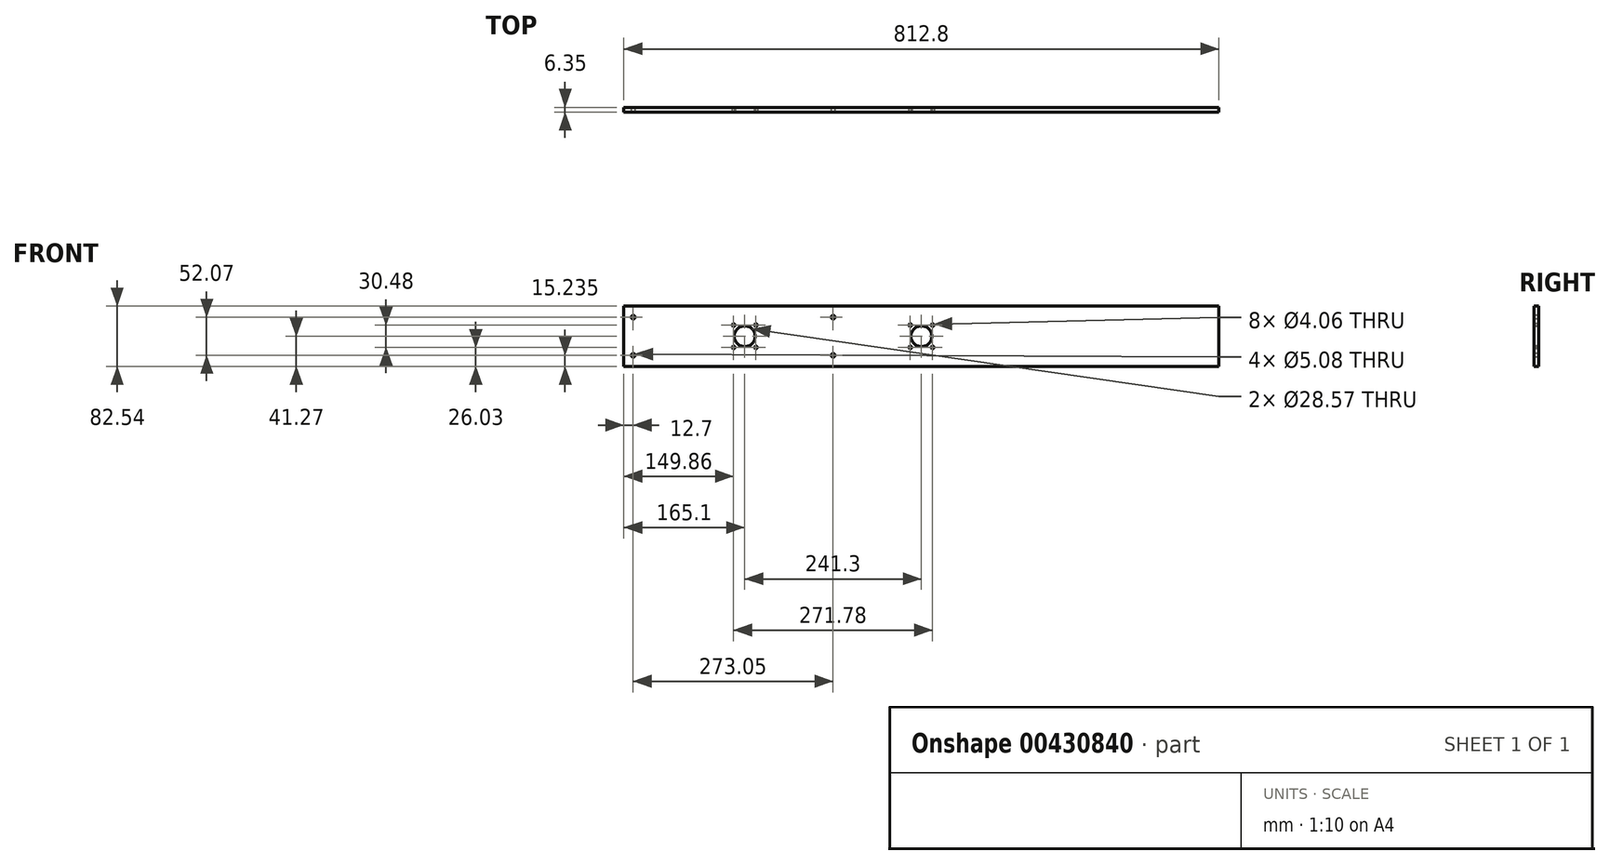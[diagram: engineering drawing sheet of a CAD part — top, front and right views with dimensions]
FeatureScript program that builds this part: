
annotation { "Feature Type Name" : "Feature", "Feature Type Description" : "" }
export const myFeature = defineFeature(function(context is Context, id is Id, definition is map)
    precondition{}
    {
        {
            var Q0;
            Q0=qCreatedBy(makeId("Front.planeOp"),FACE);
            var sketch = newSketch(context, id + "F0", { "sketchPlane" : qUnion([Q0])});
            skLineSegment(sketch, "E0.bottom", {"start": v(406.4, 41.28) * mm, "end": v(-406.4, 41.28) * mm});
            skLineSegment(sketch, "E0.top", {"start": v(406.4, -41.28) * mm, "end": v(-406.4, -41.28) * mm});
            skLineSegment(sketch, "E0.left", {"start": v(406.4, 41.28) * mm, "end": v(406.4, -41.28) * mm});
            skLineSegment(sketch, "E0.right", {"start": v(-406.4, 41.28) * mm, "end": v(-406.4, -41.28) * mm});
            skPoint(sketch, "E0.middle", {"position": v(0, 0) * mm});
            skSolve(sketch);
        }
        {
            var Q0;
            Q0=makeQuery(id+"F0.imprint","IMPRINT",FACE,{"disambiguationData":[TD([[makeQuery(id+"F0.imprint","IMPRINT",EDGE,{"derivedFrom":sQuery(id+"F0.wireOp",EDGE,"E0.bottom")}),1.0]])]});
            extrude(context, id + "F1", {"entities" : qUnion([Q0]), "depth" : 6.35 * mm});
        }
        {
            var Q0;
            Q0=makeQuery(id+"F1.opExtrude","CAP_FACE",FACE,{"disambiguationData":[OSD([sQuery(id+"F0.wireOp",EDGE,"E0.bottom"),sQuery(id+"F0.wireOp",EDGE,"E0.top"),sQuery(id+"F0.wireOp",EDGE,"E0.left"),sQuery(id+"F0.wireOp",EDGE,"E0.right")])],"isStart":false});
            var sketch = newSketch(context, id + "F2", { "sketchPlane" : qUnion([Q0])});
            skLineSegment(sketch, "E1", {"start": v(-406.4, 0) * mm, "end": v(-241.3, 0) * mm});
            skLineSegment(sketch, "E2", {"start": v(-241.3, 0) * mm, "end": v(-241.3, 15.24) * mm});
            skLineSegment(sketch, "E3", {"start": v(-241.3, 15.24) * mm, "end": v(-256.54, 15.24) * mm});
            skLineSegment(sketch, "E4", {"start": v(-256.54, 15.24) * mm, "end": v(-256.54, -15.24) * mm});
            skLineSegment(sketch, "E5", {"start": v(-256.54, -15.24) * mm, "end": v(-226.06, -15.24) * mm});
            skLineSegment(sketch, "E6", {"start": v(-226.06, -15.24) * mm, "end": v(-226.06, 15.24) * mm});
            skCircle(sketch, "E7", {"center": v(-256.54, 15.24) * mm, "radius": 2.03 * mm});
            skCircle(sketch, "E8", {"center": v(-256.54, -15.24) * mm, "radius": 2.03 * mm});
            skCircle(sketch, "E9", {"center": v(-226.06, -15.24) * mm, "radius": 2.03 * mm});
            skCircle(sketch, "E10", {"center": v(-226.06, 15.24) * mm, "radius": 2.03 * mm});
            skCircle(sketch, "E11", {"center": v(-241.3, 0) * mm, "radius": 14.29 * mm});
            skLineSegment(sketch, "E12", {"start": v(0, 0) * mm, "end": v(0, 15.24) * mm});
            skLineSegment(sketch, "E13", {"start": v(0, 15.24) * mm, "end": v(-15.24, 15.24) * mm});
            skLineSegment(sketch, "E14", {"start": v(-15.24, 15.24) * mm, "end": v(-15.24, -15.24) * mm});
            skLineSegment(sketch, "E15", {"start": v(-15.24, -15.24) * mm, "end": v(15.24, -15.24) * mm});
            skLineSegment(sketch, "E16", {"start": v(15.24, -15.24) * mm, "end": v(15.24, 15.24) * mm});
            skCircle(sketch, "E17", {"center": v(-15.24, 15.24) * mm, "radius": 2.03 * mm});
            skCircle(sketch, "E18", {"center": v(-15.24, -15.24) * mm, "radius": 2.03 * mm});
            skCircle(sketch, "E19", {"center": v(15.24, -15.24) * mm, "radius": 2.03 * mm});
            skCircle(sketch, "E20", {"center": v(15.24, 15.24) * mm, "radius": 2.03 * mm});
            skCircle(sketch, "E21", {"center": v(0, 0) * mm, "radius": 14.29 * mm});
            skSolve(sketch);
        }
        {
            var Q0;
            {var subQ0=sQuery(id+"F2.wireOp",EDGE,"E4");var subQ1=sQuery(id+"F2.wireOp",EDGE,"E3");var subQ2=makeQuery(id+"F2.imprint","INTERSECT",VERTEX,{"derivedFrom":[subQ1,subQ0]});Q0=makeQuery(id+"F2.imprint","IMPRINT",FACE,{"disambiguationData":[TD([[makeQuery(id+"F2.imprint","IMPRINT",EDGE,{"disambiguationData":[TD([[subQ2,1.0]])],"derivedFrom":subQ1}),-1.0]])]});}
            var Q1;
            {var subQ0=sQuery(id+"F2.wireOp",EDGE,"E4");var subQ1=sQuery(id+"F2.wireOp",EDGE,"E3");var subQ2=makeQuery(id+"F2.imprint","INTERSECT",VERTEX,{"derivedFrom":[subQ1,subQ0]});Q1=makeQuery(id+"F2.imprint","IMPRINT",FACE,{"disambiguationData":[TD([[makeQuery(id+"F2.imprint","IMPRINT",EDGE,{"disambiguationData":[TD([[subQ2,1.0]])],"derivedFrom":subQ1}),1.0]])]});}
            var Q2;
            {var subQ0=sQuery(id+"F2.wireOp",EDGE,"E2");var subQ1=sQuery(id+"F2.wireOp",EDGE,"E1");var subQ2=makeQuery(id+"F2.imprint","INTERSECT",VERTEX,{"derivedFrom":[subQ1,subQ0]});Q2=makeQuery(id+"F2.imprint","IMPRINT",FACE,{"disambiguationData":[TD([[makeQuery(id+"F2.imprint","IMPRINT",EDGE,{"disambiguationData":[TD([[subQ2,1.0]])],"derivedFrom":subQ1}),-1.0]])]});}
            var Q3;
            {var subQ0=sQuery(id+"F2.wireOp",EDGE,"E2");var subQ1=sQuery(id+"F2.wireOp",EDGE,"E1");var subQ2=makeQuery(id+"F2.imprint","INTERSECT",VERTEX,{"derivedFrom":[subQ1,subQ0]});Q3=makeQuery(id+"F2.imprint","IMPRINT",FACE,{"disambiguationData":[TD([[makeQuery(id+"F2.imprint","IMPRINT",EDGE,{"disambiguationData":[TD([[subQ2,1.0]])],"derivedFrom":subQ1}),1.0]])]});}
            var Q4;
            {var subQ0=sQuery(id+"F2.wireOp",EDGE,"E5");var subQ1=sQuery(id+"F2.wireOp",EDGE,"E4");var subQ2=makeQuery(id+"F2.imprint","INTERSECT",VERTEX,{"derivedFrom":[subQ1,subQ0]});Q4=makeQuery(id+"F2.imprint","IMPRINT",FACE,{"disambiguationData":[TD([[makeQuery(id+"F2.imprint","IMPRINT",EDGE,{"disambiguationData":[TD([[subQ2,1.0]])],"derivedFrom":subQ1}),-1.0]])]});}
            var Q5;
            {var subQ0=sQuery(id+"F2.wireOp",EDGE,"E5");var subQ1=sQuery(id+"F2.wireOp",EDGE,"E4");var subQ2=makeQuery(id+"F2.imprint","INTERSECT",VERTEX,{"derivedFrom":[subQ1,subQ0]});Q5=makeQuery(id+"F2.imprint","IMPRINT",FACE,{"disambiguationData":[TD([[makeQuery(id+"F2.imprint","IMPRINT",EDGE,{"disambiguationData":[TD([[subQ2,1.0]])],"derivedFrom":subQ1}),1.0]])]});}
            var Q6;
            {var subQ0=sQuery(id+"F2.wireOp",EDGE,"E6");var subQ1=sQuery(id+"F2.wireOp",EDGE,"E5");var subQ2=makeQuery(id+"F2.imprint","INTERSECT",VERTEX,{"derivedFrom":[subQ1,subQ0]});Q6=makeQuery(id+"F2.imprint","IMPRINT",FACE,{"disambiguationData":[TD([[makeQuery(id+"F2.imprint","IMPRINT",EDGE,{"disambiguationData":[TD([[subQ2,1.0]])],"derivedFrom":subQ1}),-1.0]])]});}
            var Q7;
            {var subQ0=sQuery(id+"F2.wireOp",EDGE,"E6");var subQ1=sQuery(id+"F2.wireOp",EDGE,"E5");var subQ2=makeQuery(id+"F2.imprint","INTERSECT",VERTEX,{"derivedFrom":[subQ1,subQ0]});Q7=makeQuery(id+"F2.imprint","IMPRINT",FACE,{"disambiguationData":[TD([[makeQuery(id+"F2.imprint","IMPRINT",EDGE,{"disambiguationData":[TD([[subQ2,1.0]])],"derivedFrom":subQ1}),1.0]])]});}
            var Q8;
            Q8=makeQuery(id+"F2.imprint","IMPRINT",FACE,{"disambiguationData":[TD([[makeQuery(id+"F2.imprint","IMPRINT",EDGE,{"derivedFrom":sQuery(id+"F2.wireOp",EDGE,"E10")}),1.0]])]});
            var Q9;
            Q9=makeQuery(id+"F2.imprint","IMPRINT",FACE,{"disambiguationData":[TD([[makeQuery(id+"F2.imprint","IMPRINT",EDGE,{"derivedFrom":sQuery(id+"F2.wireOp",EDGE,"E21")}),1.0]])]});
            var Q10;
            {var subQ0=sQuery(id+"F2.wireOp",EDGE,"E16");var subQ1=sQuery(id+"F2.wireOp",EDGE,"E15");var subQ2=makeQuery(id+"F2.imprint","INTERSECT",VERTEX,{"derivedFrom":[subQ1,subQ0]});Q10=makeQuery(id+"F2.imprint","IMPRINT",FACE,{"disambiguationData":[TD([[makeQuery(id+"F2.imprint","IMPRINT",EDGE,{"disambiguationData":[TD([[subQ2,1.0]])],"derivedFrom":subQ1}),-1.0]])]});}
            var Q11;
            {var subQ0=sQuery(id+"F2.wireOp",EDGE,"E16");var subQ1=sQuery(id+"F2.wireOp",EDGE,"E15");var subQ2=makeQuery(id+"F2.imprint","INTERSECT",VERTEX,{"derivedFrom":[subQ1,subQ0]});Q11=makeQuery(id+"F2.imprint","IMPRINT",FACE,{"disambiguationData":[TD([[makeQuery(id+"F2.imprint","IMPRINT",EDGE,{"disambiguationData":[TD([[subQ2,1.0]])],"derivedFrom":subQ1}),1.0]])]});}
            var Q12;
            Q12=makeQuery(id+"F2.imprint","IMPRINT",FACE,{"disambiguationData":[TD([[makeQuery(id+"F2.imprint","IMPRINT",EDGE,{"derivedFrom":sQuery(id+"F2.wireOp",EDGE,"E20")}),1.0]])]});
            var Q13;
            {var subQ0=sQuery(id+"F2.wireOp",EDGE,"E14");var subQ1=sQuery(id+"F2.wireOp",EDGE,"E13");var subQ2=makeQuery(id+"F2.imprint","INTERSECT",VERTEX,{"derivedFrom":[subQ1,subQ0]});Q13=makeQuery(id+"F2.imprint","IMPRINT",FACE,{"disambiguationData":[TD([[makeQuery(id+"F2.imprint","IMPRINT",EDGE,{"disambiguationData":[TD([[subQ2,1.0]])],"derivedFrom":subQ1}),-1.0]])]});}
            var Q14;
            {var subQ0=sQuery(id+"F2.wireOp",EDGE,"E14");var subQ1=sQuery(id+"F2.wireOp",EDGE,"E13");var subQ2=makeQuery(id+"F2.imprint","INTERSECT",VERTEX,{"derivedFrom":[subQ1,subQ0]});Q14=makeQuery(id+"F2.imprint","IMPRINT",FACE,{"disambiguationData":[TD([[makeQuery(id+"F2.imprint","IMPRINT",EDGE,{"disambiguationData":[TD([[subQ2,1.0]])],"derivedFrom":subQ1}),1.0]])]});}
            var Q15;
            {var subQ0=sQuery(id+"F2.wireOp",EDGE,"E15");var subQ1=sQuery(id+"F2.wireOp",EDGE,"E14");var subQ2=makeQuery(id+"F2.imprint","INTERSECT",VERTEX,{"derivedFrom":[subQ1,subQ0]});Q15=makeQuery(id+"F2.imprint","IMPRINT",FACE,{"disambiguationData":[TD([[makeQuery(id+"F2.imprint","IMPRINT",EDGE,{"disambiguationData":[TD([[subQ2,1.0]])],"derivedFrom":subQ1}),-1.0]])]});}
            var Q16;
            {var subQ0=sQuery(id+"F2.wireOp",EDGE,"E15");var subQ1=sQuery(id+"F2.wireOp",EDGE,"E14");var subQ2=makeQuery(id+"F2.imprint","INTERSECT",VERTEX,{"derivedFrom":[subQ1,subQ0]});Q16=makeQuery(id+"F2.imprint","IMPRINT",FACE,{"disambiguationData":[TD([[makeQuery(id+"F2.imprint","IMPRINT",EDGE,{"disambiguationData":[TD([[subQ2,1.0]])],"derivedFrom":subQ1}),1.0]])]});}
            var Q17;
            Q17=makeQuery(id+"F1.opExtrude","CAP_FACE",FACE,{"disambiguationData":[OSD([sQuery(id+"F0.wireOp",EDGE,"E0.bottom"),sQuery(id+"F0.wireOp",EDGE,"E0.top"),sQuery(id+"F0.wireOp",EDGE,"E0.left"),sQuery(id+"F0.wireOp",EDGE,"E0.right")])],"isStart":true});
            extrude(context, id + "F3", {"entities" : qUnion([Q0, Q1, Q2, Q3, Q4, Q5, Q6, Q7, Q8, Q9, Q10, Q11, Q12, Q13, Q14, Q15, Q16]), "operationType" : NewBodyOperationType.REMOVE, "endBound" : BoundingType.UP_TO_SURFACE, "oppositeDirection" : true, "endBoundEntityFace" : qUnion([Q17]), "depth" : 25.4 * mm});
        }
        {
            var Q0;
            Q0=makeQuery(id+"F1.opExtrude","CAP_FACE",FACE,{"disambiguationData":[OSD([sQuery(id+"F0.wireOp",EDGE,"E0.bottom"),sQuery(id+"F0.wireOp",EDGE,"E0.top"),sQuery(id+"F0.wireOp",EDGE,"E0.left"),sQuery(id+"F0.wireOp",EDGE,"E0.right")])],"isStart":false});
            var sketch = newSketch(context, id + "F4", { "sketchPlane" : qUnion([Q0])});
            skLineSegment(sketch, "E22", {"start": v(-393.7, 41.28) * mm, "end": v(-393.7, -41.28) * mm});
            skPoint(sketch, "E23", {"position": v(-393.7, 26.04) * mm});
            skPoint(sketch, "E24", {"position": v(-393.7, -26.04) * mm});
            skCircle(sketch, "E25", {"center": v(-393.7, 26.04) * mm, "radius": 2.54 * mm});
            skCircle(sketch, "E26", {"center": v(-393.7, -26.04) * mm, "radius": 2.54 * mm});
            skLineSegment(sketch, "E27", {"start": v(-241.3, 0) * mm, "end": v(-241.3, 41.28) * mm});
            skLineSegment(sketch, "E28", {"start": v(-241.3, 41.28) * mm, "end": v(0, 41.28) * mm});
            skLineSegment(sketch, "E29", {"start": v(-120.65, 41.28) * mm, "end": v(-120.65, -41.28) * mm});
            skPoint(sketch, "E30", {"position": v(-120.65, -26.04) * mm});
            skPoint(sketch, "E31", {"position": v(-120.65, 26.04) * mm});
            skCircle(sketch, "E32", {"center": v(-120.65, -26.04) * mm, "radius": 2.54 * mm});
            skCircle(sketch, "E33", {"center": v(-120.65, 26.04) * mm, "radius": 2.54 * mm});
            skSolve(sketch);
        }
        {
            var Q0;
            Q0 = qSketchRegion(id + "F4", true);
            var Q1;
            Q1=makeQuery(id+"F1.opExtrude","CAP_FACE",FACE,{"disambiguationData":[OSD([sQuery(id+"F0.wireOp",EDGE,"E0.bottom"),sQuery(id+"F0.wireOp",EDGE,"E0.top"),sQuery(id+"F0.wireOp",EDGE,"E0.left"),sQuery(id+"F0.wireOp",EDGE,"E0.right")])],"isStart":true});
            extrude(context, id + "F5", {"entities" : qUnion([Q0]), "operationType" : NewBodyOperationType.REMOVE, "endBound" : BoundingType.UP_TO_SURFACE, "oppositeDirection" : true, "endBoundEntityFace" : qUnion([Q1]), "depth" : 25.4 * mm});
        }
    });
